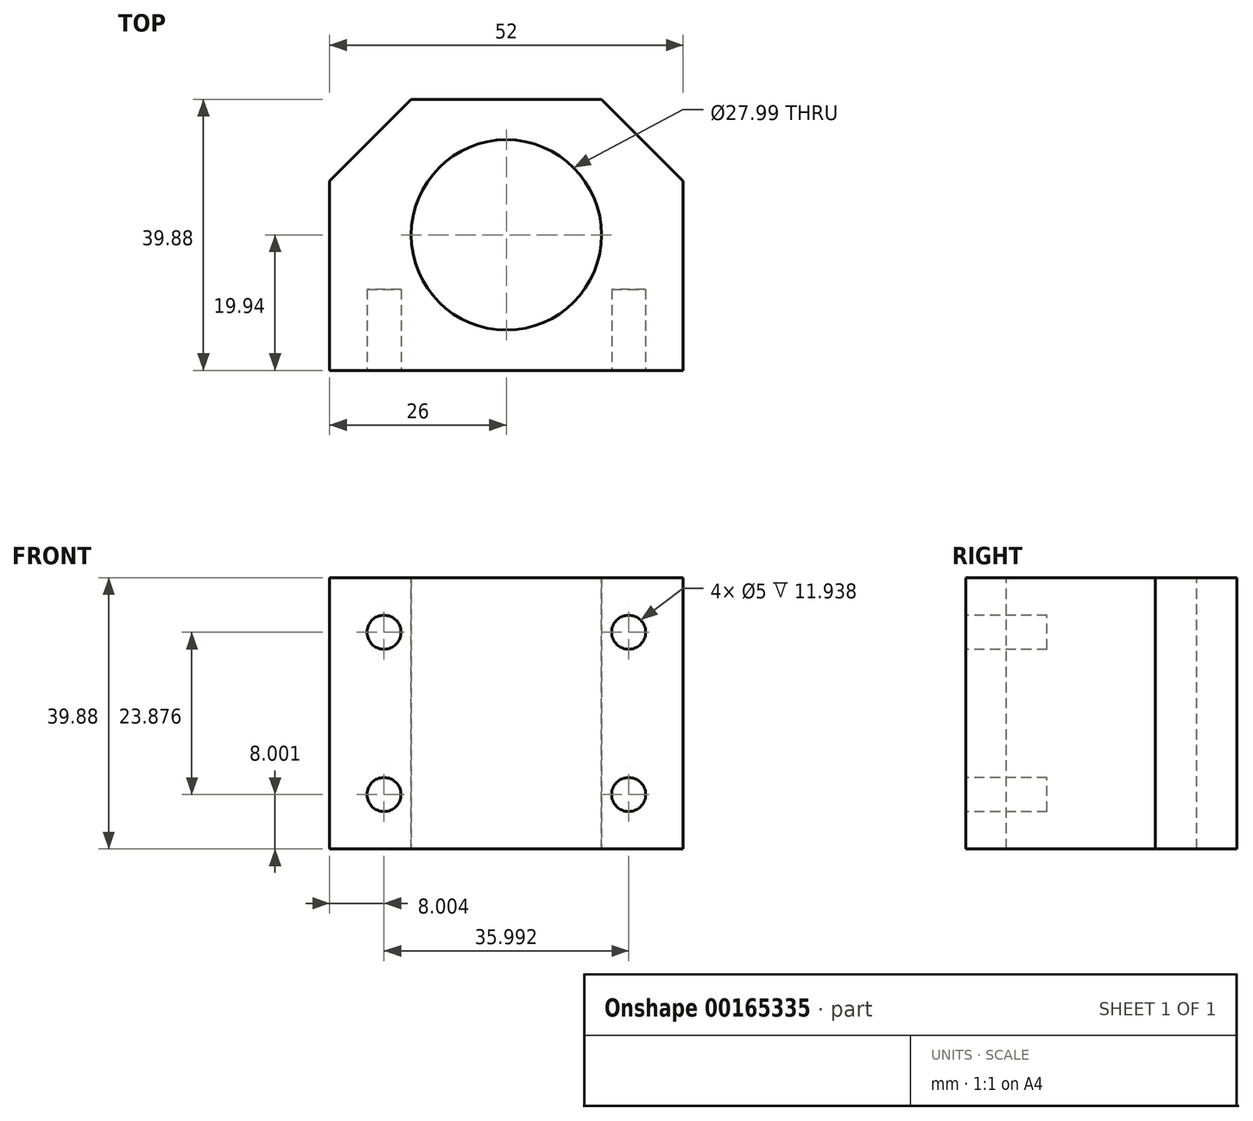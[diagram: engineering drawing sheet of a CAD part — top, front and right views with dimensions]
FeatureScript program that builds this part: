
annotation { "Feature Type Name" : "Feature", "Feature Type Description" : "" }
export const myFeature = defineFeature(function(context is Context, id is Id, definition is map)
    precondition{}
    {
        {
            var Q0;
            Q0=qCreatedBy(makeId("Top.planeOp"),FACE);
            var sketch = newSketch(context, id + "F0", { "sketchPlane" : qUnion([Q0])});
            skLineSegment(sketch, "E0.rect.bottom", {"start": v(26, -19.94) * mm, "end": v(-26, -19.94) * mm});
            skLineSegment(sketch, "E0.rect.top", {"start": v(26, 19.94) * mm, "end": v(-26, 19.94) * mm});
            skLineSegment(sketch, "E0.rect.left", {"start": v(26, -19.94) * mm, "end": v(26, 19.94) * mm});
            skLineSegment(sketch, "E0.rect.right", {"start": v(-26, -19.94) * mm, "end": v(-26, 19.94) * mm});
            skPoint(sketch, "E0.rect.middle", {"position": v(0, 0) * mm});
            skLineSegment(sketch, "E1", {"start": v(-14, 19.94) * mm, "end": v(-26, 7.95) * mm});
            skLineSegment(sketch, "E2", {"start": v(14, 19.94) * mm, "end": v(26, 7.95) * mm});
            skSolve(sketch);
        }
        {
            var Q0;
            Q0=qSketchRegion(id+"F0",true);
            extrude(context, id + "F1", {"entities" : qUnion([Q0]), "depth" : 39.88 * mm});
        }
        {
            var Q0;
            Q0=makeQuery(id+"F1.opExtrude","CAP_FACE",FACE,{"disambiguationData":[OSD([sQuery(id+"F0.wireOp",EDGE,"E0.rect.bottom"),sQuery(id+"F0.wireOp",EDGE,"E0.rect.top"),sQuery(id+"F0.wireOp",EDGE,"E0.rect.left"),sQuery(id+"F0.wireOp",EDGE,"E0.rect.right")])],"isStart":false});
            var sketch = newSketch(context, id + "F2", { "sketchPlane" : qUnion([Q0])});
            skCircle(sketch, "E3", {"center": v(0, 0) * mm, "radius": 14 * mm});
            skSolve(sketch);
        }
        {
            var Q0;
            Q0=qSketchRegion(id+"F2",true);
            extrude(context, id + "F3", {"entities" : qUnion([Q0]), "operationType" : NewBodyOperationType.REMOVE, "endBound" : BoundingType.THROUGH_ALL, "oppositeDirection" : true, "depth" : 25.4 * mm});
        }
        {
            var Q0;
            {var subQ3=sQuery(id+"F0.wireOp",EDGE,"E2");Q0=makeQuery(id+"F0.imprint","IMPRINT",FACE,{"disambiguationData":[TD([[makeQuery(id+"F0.imprint","IMPRINT",EDGE,{"derivedFrom":subQ3}),1.0]])]});}
            extrude(context, id + "F4", {"entities" : qUnion([Q0]), "operationType" : NewBodyOperationType.REMOVE, "endBound" : BoundingType.THROUGH_ALL, "depth" : 25.4 * mm});
        }
        {
            var Q0;
            {var subQ3=sQuery(id+"F0.wireOp",EDGE,"E1");Q0=makeQuery(id+"F0.imprint","IMPRINT",FACE,{"disambiguationData":[TD([[makeQuery(id+"F0.imprint","IMPRINT",EDGE,{"derivedFrom":subQ3}),-1.0]])]});}
            extrude(context, id + "F5", {"entities" : qUnion([Q0]), "operationType" : NewBodyOperationType.REMOVE, "endBound" : BoundingType.THROUGH_ALL, "depth" : 25.4 * mm});
        }
        {
            var Q0;
            Q0=makeQuery(id+"F1.opExtrude","SWEPT_FACE",FACE,{"disambiguationData":[OSD([sQuery(id+"F0.wireOp",EDGE,"E0.rect.bottom")])]});
            var sketch = newSketch(context, id + "F6", { "sketchPlane" : qUnion([Q0])});
            skLineSegment(sketch, "E4", {"start": v(26, 31.88) * mm, "end": v(-26, 31.88) * mm, "construction": true});
            skLineSegment(sketch, "E5", {"start": v(-18, 39.88) * mm, "end": v(-18, 0) * mm, "construction": true});
            skLineSegment(sketch, "E6", {"start": v(-18, 0) * mm, "end": v(-18.3, 0.31) * mm, "construction": true});
            skLineSegment(sketch, "E7", {"start": v(26, 8) * mm, "end": v(-26, 8) * mm, "construction": true});
            skLineSegment(sketch, "E8", {"start": v(18, 39.88) * mm, "end": v(18, 0) * mm, "construction": true});
            skCircle(sketch, "E9", {"center": v(18, 31.88) * mm, "radius": 2.5 * mm});
            skCircle(sketch, "E10", {"center": v(18, 8) * mm, "radius": 2.5 * mm});
            skCircle(sketch, "E11", {"center": v(-18, 8) * mm, "radius": 2.5 * mm});
            skCircle(sketch, "E12", {"center": v(-18, 31.88) * mm, "radius": 2.5 * mm});
            skLineSegment(sketch, "E13", {"start": v(0, 39.88) * mm, "end": v(0, 0) * mm, "construction": true});
            skLineSegment(sketch, "E14", {"start": v(0, 19.94) * mm, "end": v(0, 31.88) * mm, "construction": true});
            skSolve(sketch);
        }
        {
            var Q0;
            Q0=qSketchRegion(id+"F6",true);
            extrude(context, id + "F7", {"entities" : qUnion([Q0]), "operationType" : NewBodyOperationType.REMOVE, "oppositeDirection" : true, "depth" : 11.94 * mm});
        }
    });
